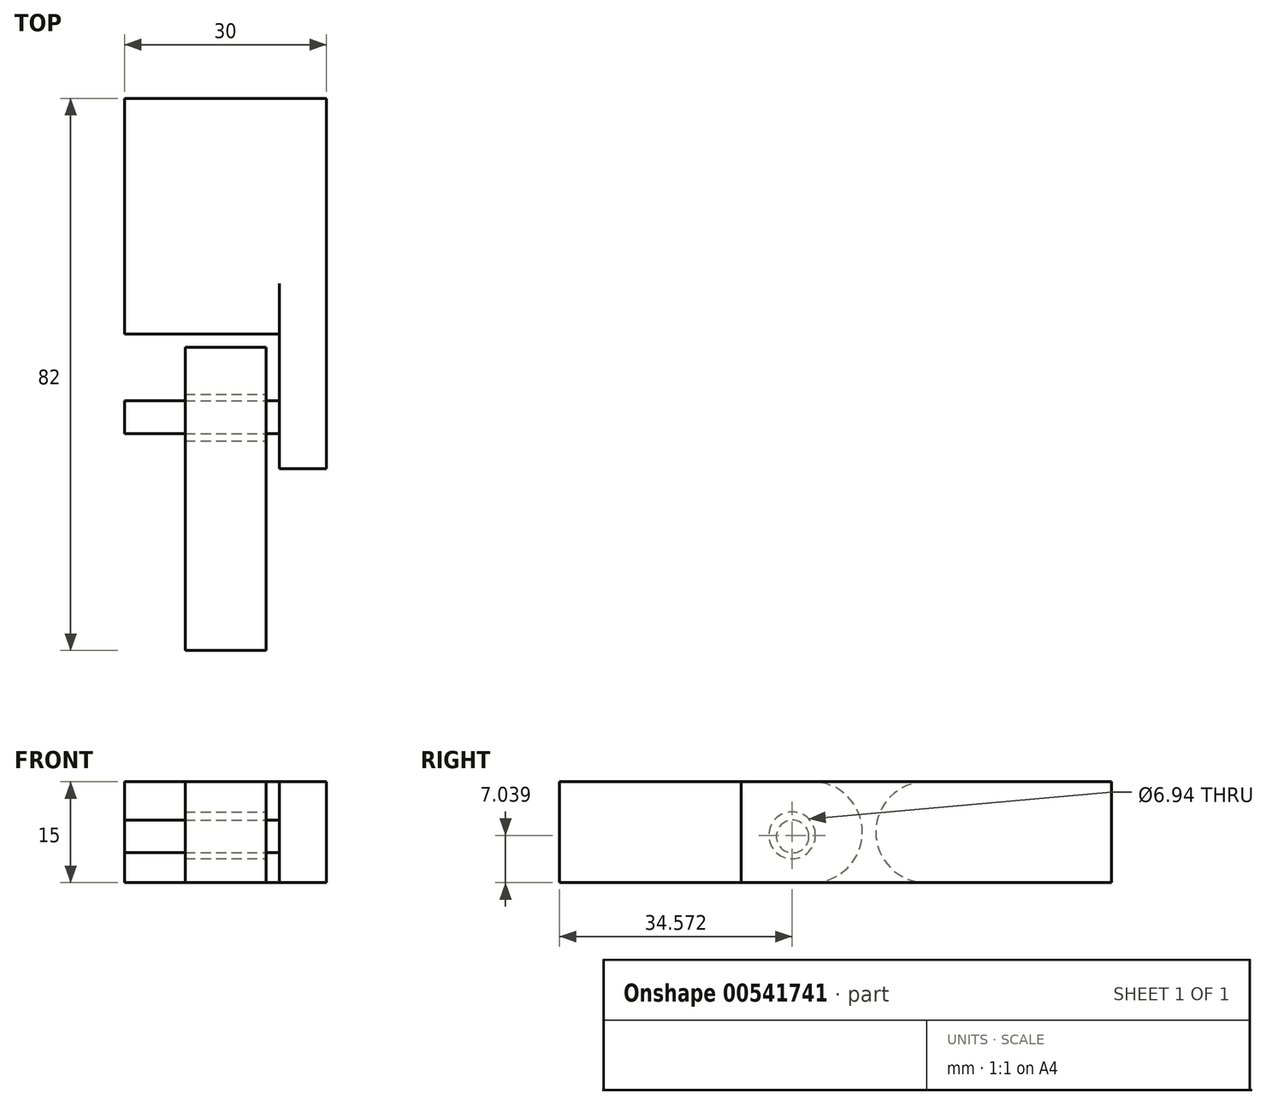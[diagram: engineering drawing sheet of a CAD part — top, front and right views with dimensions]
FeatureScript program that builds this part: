
annotation { "Feature Type Name" : "Feature", "Feature Type Description" : "" }
export const myFeature = defineFeature(function(context is Context, id is Id, definition is map)
    precondition{}
    {
        {
            var Q0;
            Q0=qCreatedBy(makeId("Top.planeOp"),FACE);
            var sketch = newSketch(context, id + "F0", { "sketchPlane" : qUnion([Q0])});
            skLineSegment(sketch, "E0.bottom", {"start": v(-15, 17.5) * mm, "end": v(15, 17.5) * mm});
            skLineSegment(sketch, "E0.top", {"start": v(-15, -17.5) * mm, "end": v(15, -17.5) * mm});
            skLineSegment(sketch, "E0.left", {"start": v(-15, 17.5) * mm, "end": v(-15, -17.5) * mm});
            skLineSegment(sketch, "E0.right", {"start": v(15, 17.5) * mm, "end": v(15, -17.5) * mm});
            skPoint(sketch, "E0.middle", {"position": v(0, 0) * mm});
            skLineSegment(sketch, "E1.bottom", {"start": v(-15, -17.5) * mm, "end": v(-8, -17.5) * mm});
            skLineSegment(sketch, "E1.top", {"start": v(-15, -37.5) * mm, "end": v(-8, -37.5) * mm});
            skLineSegment(sketch, "E1.left", {"start": v(-15, -17.5) * mm, "end": v(-15, -37.5) * mm});
            skLineSegment(sketch, "E1.right", {"start": v(-8, -17.5) * mm, "end": v(-8, -37.5) * mm});
            skLineSegment(sketch, "E2", {"start": v(0, 40.26) * mm, "end": v(0, -50.75) * mm, "construction": true});
            skLineSegment(sketch, "E3.MirrorCS", {"start": v(8, -17.5) * mm, "end": v(8, -37.5) * mm});
            skLineSegment(sketch, "E4.MirrorCS", {"start": v(15, -17.5) * mm, "end": v(15, -37.5) * mm});
            skLineSegment(sketch, "E5.MirrorCS", {"start": v(15, -37.5) * mm, "end": v(8, -37.5) * mm});
            skSolve(sketch);
        }
        {
            var Q0;
            Q0=makeQuery(id+"F0.imprint","IMPRINT",FACE,{"disambiguationData":[TD([[makeQuery(id+"F0.imprint","IMPRINT",EDGE,{"derivedFrom":sQuery(id+"F0.wireOp",EDGE,"E0.bottom")}),-1.0]])]});
            var Q1;
            Q1=makeQuery(id+"F0.imprint","IMPRINT",FACE,{"disambiguationData":[TD([[makeQuery(id+"F0.imprint","IMPRINT",EDGE,{"derivedFrom":sQuery(id+"F0.wireOp",EDGE,"E1.bottom")}),-1.0]])]});
            var Q2;
            {var subQ2=sQuery(id+"F0.wireOp",EDGE,"E3.MirrorCS");Q2=makeQuery(id+"F0.imprint","IMPRINT",FACE,{"disambiguationData":[TD([[makeQuery(id+"F0.imprint","IMPRINT",EDGE,{"derivedFrom":subQ2}),1.0]])]});}
            extrude(context, id + "F1", {"entities" : qUnion([Q0, Q1, Q2]), "depth" : 15 * mm, "offsetDistance" : 25 * mm});
        }
        {
            var Q0;
            Q0=qCreatedBy(makeId("Top.planeOp"),FACE);
            var sketch = newSketch(context, id + "F2", { "sketchPlane" : qUnion([Q0])});
            skLineSegment(sketch, "E6.bottom", {"start": v(-6, -19.5) * mm, "end": v(6, -19.5) * mm});
            skLineSegment(sketch, "E6.top", {"start": v(-6, -64.5) * mm, "end": v(6, -64.5) * mm});
            skLineSegment(sketch, "E6.left", {"start": v(-6, -19.5) * mm, "end": v(-6, -64.5) * mm});
            skLineSegment(sketch, "E6.right", {"start": v(6, -19.5) * mm, "end": v(6, -64.5) * mm});
            skPoint(sketch, "E6.middle", {"position": v(0, -42) * mm});
            skSolve(sketch);
        }
        {
            var Q0;
            Q0=makeQuery(id+"F2.imprint","IMPRINT",FACE,{"disambiguationData":[TD([[makeQuery(id+"F2.imprint","IMPRINT",EDGE,{"derivedFrom":sQuery(id+"F2.wireOp",EDGE,"E6.bottom")}),-1.0]])]});
            extrude(context, id + "F3", {"entities" : qUnion([Q0]), "depth" : 15 * mm, "offsetDistance" : 25 * mm});
        }
        {
            var Q0;
            Q0=makeQuery(id+"F3.opExtrude","SWEPT_FACE",FACE,{"disambiguationData":[OSD([sQuery(id+"F2.wireOp",EDGE,"E6.right")])]});
            var sketch = newSketch(context, id + "F4", { "sketchPlane" : qUnion([Q0])});
            skCircle(sketch, "E7", {"center": v(-29.93, 7.04) * mm, "radius": 3.47 * mm});
            skSolve(sketch);
        }
        {
            var Q0;
            Q0=makeQuery(id+"F4.imprint","IMPRINT",FACE,{"disambiguationData":[TD([[makeQuery(id+"F4.imprint","IMPRINT",EDGE,{"derivedFrom":sQuery(id+"F4.wireOp",EDGE,"E7")}),1.0]])]});
            extrude(context, id + "F5", {"entities" : qUnion([Q0]), "operationType" : NewBodyOperationType.REMOVE, "endBound" : BoundingType.UP_TO_NEXT, "oppositeDirection" : true, "depth" : 25 * mm, "offsetDistance" : 25 * mm});
        }
        {
            var Q0;
            Q0=makeQuery(id+"F1.opExtrude","SWEPT_FACE",FACE,{"disambiguationData":[OSD([sQuery(id+"F0.wireOp",EDGE,"E0.right"),sQuery(id+"F0.wireOp",EDGE,"E4.MirrorCS")])]});
            var sketch = newSketch(context, id + "F6", { "sketchPlane" : qUnion([Q0])});
            skCircle(sketch, "E8", {"center": v(-29.85, 6.87) * mm, "radius": 2.42 * mm});
            skSolve(sketch);
        }
        {
            var Q0;
            Q0=makeQuery(id+"F6.imprint","IMPRINT",FACE,{"disambiguationData":[TD([[makeQuery(id+"F6.imprint","IMPRINT",EDGE,{"derivedFrom":sQuery(id+"F6.wireOp",EDGE,"E8")}),1.0]])]});
            var Q1;
            Q1=makeQuery(id+"F1.opExtrude","SWEPT_FACE",FACE,{"disambiguationData":[OSD([sQuery(id+"F0.wireOp",EDGE,"E0.left"),sQuery(id+"F0.wireOp",EDGE,"E1.left")])]});
            extrude(context, id + "F7", {"entities" : qUnion([Q0]), "operationType" : NewBodyOperationType.ADD, "endBound" : BoundingType.UP_TO_SURFACE, "oppositeDirection" : true, "depth" : 25 * mm, "endBoundEntityFace" : qUnion([Q1]), "offsetDistance" : 25 * mm});
        }
        {
            var Q0;
            Q0=makeQuery(id+"F1.opExtrude","CAP_EDGE",EDGE,{"disambiguationData":[OSD([sQuery(id+"F0.wireOp",EDGE,"E0.top")])],"isStart":true});
            var Q1;
            Q1=makeQuery(id+"F1.opExtrude","CAP_EDGE",EDGE,{"disambiguationData":[OSD([sQuery(id+"F0.wireOp",EDGE,"E0.top")])],"isStart":false});
            var Q2;
            Q2=makeQuery(id+"F3.opExtrude","CAP_EDGE",EDGE,{"disambiguationData":[OSD([sQuery(id+"F2.wireOp",EDGE,"E6.bottom")])],"isStart":true});
            var Q3;
            Q3=makeQuery(id+"F3.opExtrude","CAP_EDGE",EDGE,{"disambiguationData":[OSD([sQuery(id+"F2.wireOp",EDGE,"E6.bottom")])],"isStart":false});
            fillet(context, id + "F8", {"entities" : qUnion([Q0, Q1, Q2, Q3]), "radius" : 7.5 * mm, "tangentPropagation" : true, "allowEdgeOverflow" : false});
        }
    });
